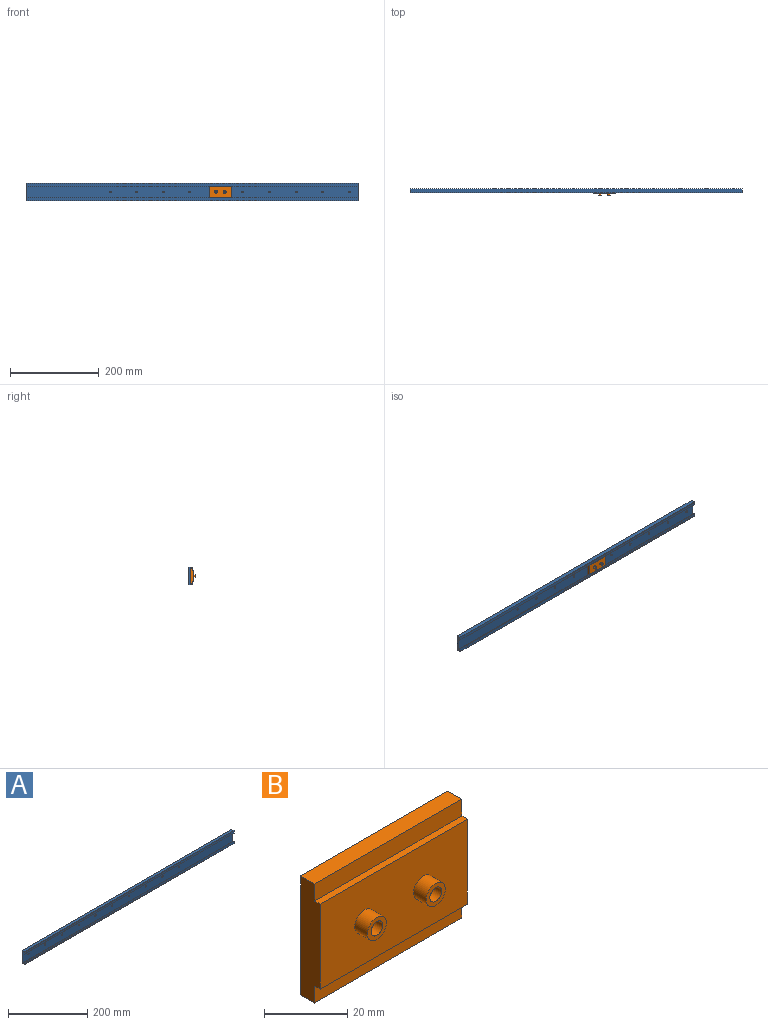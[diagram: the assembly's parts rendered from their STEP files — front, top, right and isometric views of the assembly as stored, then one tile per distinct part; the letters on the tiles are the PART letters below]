
ASSEMBLY  parts=2 mates=1
PART A: 24 faces, bbox 750x8.7x40 mm
  f0: plane 750x5mm, normal (0,1,0), area 3750mm2, adj f1,f11,f12,f13
  f1: plane 750x1mm, normal (0,0,1), area 750mm2, adj f0,f2,f12,f13
  f2: plane 750x7.5mm, normal (0,-1,0), area 5625mm2, adj f1,f3,f12,f13
  f3: plane 750x8.7mm, normal (0,0,-1), area 6525mm2, adj f2,f4,f12,f13
  f4: plane 750x40mm, normal (0,1,0), area 29841mm2, adj f3,f5,f12,f13,f14,f15,f16,f17
  f5: plane 750x8.7mm, normal (0,0,1), area 6525mm2, adj f4,f6,f12,f13
  f6: plane 750x7.5mm, normal (0,-1,0), area 5625mm2, adj f5,f7,f12,f13
  f7: plane 750x1mm, normal (0,0,-1), area 750mm2, adj f6,f8,f12,f13
  f8: plane 750x5mm, normal (0,1,0), area 3750mm2, adj f7,f9,f12,f13
  f9: plane 750x4.8mm, normal (0,0,-1), area 3600mm2, adj f8,f10,f12,f13
  f10: plane 750x35mm, normal (0,-1,0), area 26091mm2, adj f9,f11,f12,f13,f14,f15,f16,f17
  f11: plane 750x4.8mm, normal (0,0,1), area 3600mm2, adj f0,f10,f12,f13
  f12: plane 40x8.7mm, normal (1,0,0), area 155mm2, adj f0,f1,f2,f3,f4,f5,f6,f7
  f13: plane 40x8.7mm, normal (-1,0,0), area 155mm2, adj f0,f1,f2,f3,f4,f5,f6,f7
  f14: cylinder r=2.25mm len=4.5mm, axis (0,1,0), area 41mm2, adj f4,f10
  f15: cylinder r=2.25mm len=4.5mm, axis (0,1,0), area 41mm2, adj f4,f10
  f16: cylinder r=2.25mm len=4.5mm, axis (0,1,0), area 41mm2, adj f4,f10
  f17: cylinder r=2.25mm len=4.5mm, axis (0,1,0), area 41mm2, adj f4,f10
  f18: cylinder r=2.25mm len=4.5mm, axis (0,1,0), area 41mm2, adj f4,f10
  f19: cylinder r=2.25mm len=4.5mm, axis (0,1,0), area 41mm2, adj f4,f10
  f20: cylinder r=2.25mm len=4.5mm, axis (0,1,0), area 41mm2, adj f4,f10
  f21: cylinder r=2.25mm len=4.5mm, axis (0,1,0), area 41mm2, adj f4,f10
  f22: cylinder r=2.25mm len=4.5mm, axis (0,1,0), area 41mm2, adj f4,f10
  f23: cylinder r=2.25mm len=4.5mm, axis (0,1,0), area 41mm2, adj f4,f10
PART B: 18 faces, bbox 50x10.9x35 mm
  f0: plane 50x1.8mm, normal (0,0,-1), area 90mm2, adj f1,f7,f8,f9
  f1: plane 50x5mm, normal (0,-1,0), area 250mm2, adj f0,f2,f8,f9
  f2: plane 50x4.8mm, normal (0,0,-1), area 240mm2, adj f1,f3,f8,f9
  f3: plane 50x35mm, normal (0,1,0), area 1750mm2, adj f2,f4,f8,f9
  f4: plane 50x4.8mm, normal (0,0,1), area 240mm2, adj f3,f5,f8,f9
  f5: plane 50x5mm, normal (0,-1,0), area 250mm2, adj f4,f6,f8,f9
  f6: plane 50x1.8mm, normal (0,0,1), area 90mm2, adj f5,f7,f8,f9
  f7: plane 50x25mm, normal (0,-1,0), area 1183.6mm2, adj f0,f6,f8,f9,f11,f15
  f8: plane 35x6.6mm, normal (-1,0,0), area 213mm2, adj f0,f1,f2,f3,f4,f5,f6,f7
  f9: plane 35x6.6mm, normal (1,0,0), area 213mm2, adj f0,f1,f2,f3,f4,f5,f6,f7
  f10: cylinder r=2mm len=4.3mm, axis (0,1,0), area 54mm2, adj f12,f13
  f11: cylinder r=3.25mm len=6.5mm, axis (0,1,0), area 87.8mm2, adj f7,f12
  f12: plane 6.5x6.5mm, normal (0,-1,0), area 20.6mm2, adj f10,f11
  f13: plane 4x4mm, normal (0,-1,0), area 12.6mm2, adj f10
  f14: cylinder r=2mm len=4.3mm, axis (0,1,0), area 54mm2, adj f16,f17
  f15: cylinder r=3.25mm len=6.5mm, axis (0,1,0), area 87.8mm2, adj f7,f16
  f16: plane 6.5x6.5mm, normal (0,-1,0), area 20.6mm2, adj f14,f15
  f17: plane 4x4mm, normal (0,-1,0), area 12.6mm2, adj f14
PLACE A rot(axis=(0,-1,0),180deg) t=(263.69,1.61,-634.2)mm
PLACE B t=(-22.16,1.61,190.59)mm
MATE slider A.f13 <-> B.f9  axis (1,0,0) through (263.69,4.71,-221.81)mm
